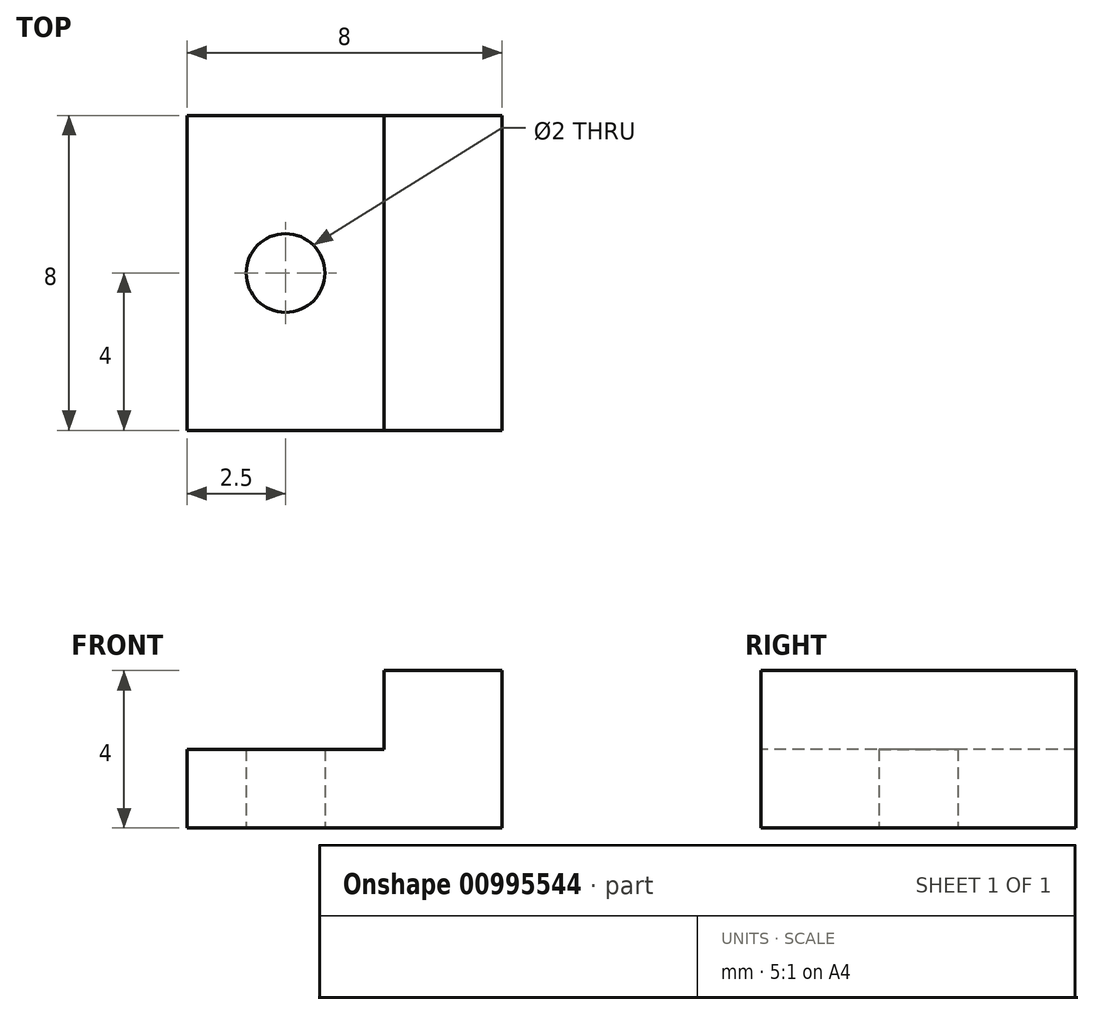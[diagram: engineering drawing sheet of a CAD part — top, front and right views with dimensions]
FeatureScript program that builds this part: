
annotation { "Feature Type Name" : "Feature", "Feature Type Description" : "" }
export const myFeature = defineFeature(function(context is Context, id is Id, definition is map)
    precondition{}
    {
        {
            var Q0;
            Q0=qCreatedBy(makeId("Top.planeOp"),FACE);
            var sketch = newSketch(context, id + "F0", { "sketchPlane" : qUnion([Q0])});
            skLineSegment(sketch, "E0.bottom", {"start": v(4, 4) * mm, "end": v(-4, 4) * mm});
            skLineSegment(sketch, "E0.top", {"start": v(4, -4) * mm, "end": v(-4, -4) * mm});
            skLineSegment(sketch, "E0.left", {"start": v(4, 4) * mm, "end": v(4, -4) * mm});
            skLineSegment(sketch, "E0.right", {"start": v(-4, 4) * mm, "end": v(-4, -4) * mm});
            skPoint(sketch, "E0.middle", {"position": v(0, 0) * mm});
            skCircle(sketch, "E1", {"center": v(-1.5, 0) * mm, "radius": 1 * mm});
            skSolve(sketch);
        }
        {
            var Q0;
            Q0=makeQuery(id+"F0.imprint","IMPRINT",FACE,{"disambiguationData":[TD([[makeQuery(id+"F0.imprint","IMPRINT",EDGE,{"derivedFrom":sQuery(id+"F0.wireOp",EDGE,"E0.bottom")}),1.0]])]});
            extrude(context, id + "F1", {"entities" : qUnion([Q0]), "depth" : 2 * mm, "offsetDistance" : 25 * mm});
        }
        {
            var Q0;
            Q0=makeQuery(id+"F1.opExtrude","CAP_FACE",FACE,{"disambiguationData":[OSD([sQuery(id+"F0.wireOp",EDGE,"E0.bottom"),sQuery(id+"F0.wireOp",EDGE,"E0.top"),sQuery(id+"F0.wireOp",EDGE,"E0.left"),sQuery(id+"F0.wireOp",EDGE,"E0.right"),sQuery(id+"F0.wireOp",EDGE,"uyGaWrKq-reT5-tSey-57RI-9wQZJy4RE7cU"),sQuery(id+"F0.wireOp",EDGE,"E1")])],"isStart":false});
            var sketch = newSketch(context, id + "F2", { "sketchPlane" : qUnion([Q0])});
            skLineSegment(sketch, "E2.bottom", {"start": v(4, 4) * mm, "end": v(1, 4) * mm});
            skLineSegment(sketch, "E2.top", {"start": v(4, -4) * mm, "end": v(1, -4) * mm});
            skLineSegment(sketch, "E2.left", {"start": v(4, 4) * mm, "end": v(4, -4) * mm});
            skLineSegment(sketch, "E2.right", {"start": v(1, 4) * mm, "end": v(1, -4) * mm});
            skSolve(sketch);
        }
        {
            var Q0;
            Q0=makeQuery(id+"F2.imprint","IMPRINT",FACE,{"disambiguationData":[TD([[makeQuery(id+"F2.imprint","IMPRINT",EDGE,{"derivedFrom":sQuery(id+"F2.wireOp",EDGE,"E2.bottom")}),1.0]])]});
            extrude(context, id + "F3", {"entities" : qUnion([Q0]), "operationType" : NewBodyOperationType.ADD, "depth" : 2 * mm, "offsetDistance" : 25 * mm});
        }
    });
